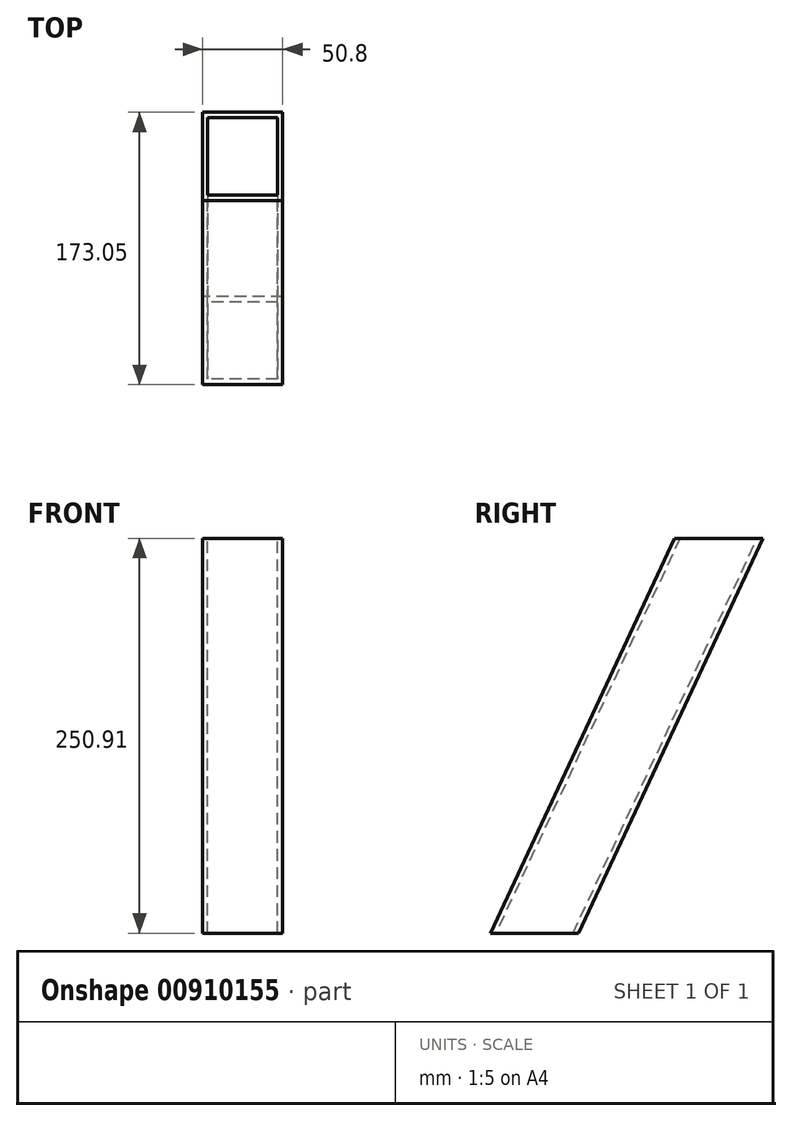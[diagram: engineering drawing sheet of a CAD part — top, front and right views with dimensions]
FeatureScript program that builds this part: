
annotation { "Feature Type Name" : "Feature", "Feature Type Description" : "" }
export const myFeature = defineFeature(function(context is Context, id is Id, definition is map)
    precondition{}
    {
        {
            var Q0;
            Q0=qCreatedBy(makeId("Right.planeOp"),FACE);
            var sketch = newSketch(context, id + "F0", { "sketchPlane" : qUnion([Q0])});
            skLineSegment(sketch, "E0", {"start": v(117, 214.48) * mm, "end": v(60.95, 214.48) * mm});
            skLineSegment(sketch, "E1", {"start": v(60.95, 214.48) * mm, "end": v(-56.05, -36.43) * mm});
            skLineSegment(sketch, "E2", {"start": v(-56.05, -36.43) * mm, "end": v(0, -36.43) * mm});
            skLineSegment(sketch, "E3", {"start": v(0, -36.43) * mm, "end": v(117, 214.48) * mm});
            skSolve(sketch);
        }
        {
            var Q0;
            Q0 = qSketchRegion(id + "F0", true);
            extrude(context, id + "F1", {"entities" : qUnion([Q0]), "depth" : 50.8 * mm, "offsetDistance" : 25.4 * mm});
        }
        {
            var Q0;
            Q0=makeQuery(id+"F1.opExtrude","SWEPT_FACE",FACE,{"disambiguationData":[OSD([sQuery(id+"F0.wireOp",EDGE,"E2")])]});
            var Q1;
            Q1=makeQuery(id+"F1.opExtrude","SWEPT_FACE",FACE,{"disambiguationData":[OSD([sQuery(id+"F0.wireOp",EDGE,"E0")])]});
            shell(context, id + "F2", {"entities" : qUnion([Q0, Q1]), "thickness" : 3.17 * mm});
        }
    });
